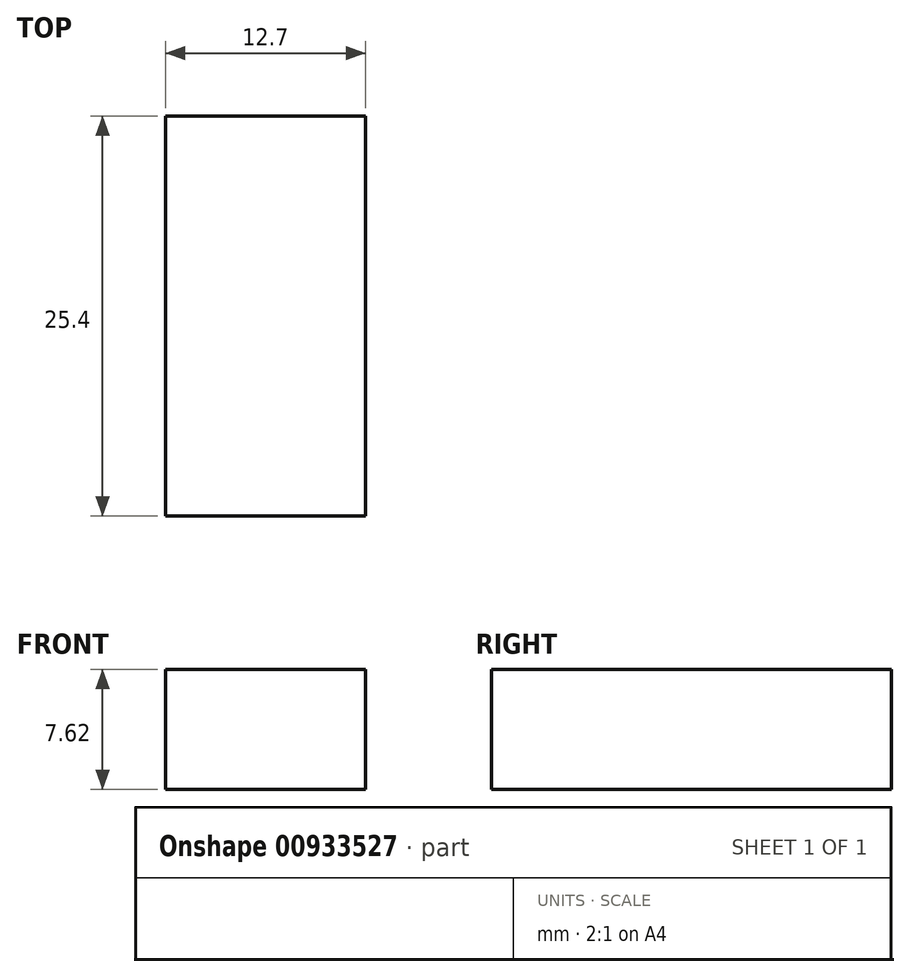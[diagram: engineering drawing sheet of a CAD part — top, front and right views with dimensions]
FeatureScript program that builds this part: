
annotation { "Feature Type Name" : "Feature", "Feature Type Description" : "" }
export const myFeature = defineFeature(function(context is Context, id is Id, definition is map)
    precondition{}
    {
        {
            var Q0;
            Q0=qCreatedBy(makeId("Front.planeOp"),FACE);
            var sketch = newSketch(context, id + "F0", { "sketchPlane" : qUnion([Q0])});
            skLineSegment(sketch, "E0", {"start": v(0, 0) * mm, "end": v(12.7, 0) * mm});
            skLineSegment(sketch, "E1", {"start": v(12.7, 0) * mm, "end": v(12.7, 7.62) * mm});
            skLineSegment(sketch, "E2", {"start": v(12.7, 7.62) * mm, "end": v(0, 7.62) * mm});
            skLineSegment(sketch, "E3", {"start": v(0, 7.62) * mm, "end": v(0, 0) * mm});
            skSolve(sketch);
        }
        {
            var Q0;
            Q0 = qSketchRegion(id + "F0", true);
            extrude(context, id + "F1", {"entities" : qUnion([Q0]), "depth" : 25.4 * mm, "offsetDistance" : 25.4 * mm});
        }
    });
